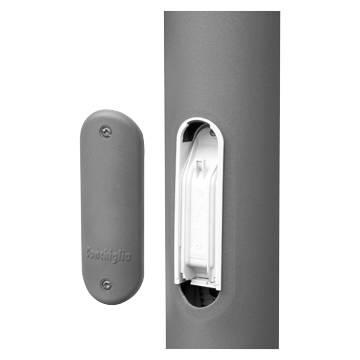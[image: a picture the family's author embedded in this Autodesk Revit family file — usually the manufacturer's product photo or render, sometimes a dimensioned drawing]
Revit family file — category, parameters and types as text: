
# Revit family: Lighting-StreetLighting-GEWISS-STREET[O3]-POLES
name_source: partatom
category: Apparecchi per illuminazione
units: mm (PartAtom-declared; Revit-internal decimal feet)

## family parameters
Condiviso = No
Host = Superficie
Numero OmniClass = 23.80.00.00
Punto di calcolo locali = No
Quota connettore circolare = Usa diametro
Sorgente d'illuminazione = No
Taglio con vuoti quando caricato = No
Tipo di parte = Normale
Titolo OmniClass = Electric Power and Lighting

## types (5) — shared parameters
Altezza palo = 9800 mm  [stored 32.1522 ft]
Catalogue = LIGHTING
Catalogue Range = STREET [O3]
Colour = Graphite grey
Diametro = 60 mm  [stored 0.19685 ft]
Diametro inferiore = 158 mm  [stored 0.518373 ft]
Electrocod = 240
Finishing = Painted
IDF = d4c518be-a0db-4a63-a47f-d3abfb27bd65
IDT = d3b2aa7b-33ea-43be-8ddf-58a48c27c07e
Immagine tipo = GW84096.jpg
Material = Galvanised steel
Palo = <Per categoria>
Produttore = GEWISS S.p.A.
Prospetto di default = 1219 mm
SEO = Pole
Technical sheet = https://www.gewiss.com
Top diameter (mm) = 60
Type: = Conical
URL = https://www.gewiss.com
Version file RFA = 20.11

## per-type parameters (varying)
| type | Base diameter (mm) | Descrizione | EAN code | Modello | Planting (m) | Total length (m) | Weight (kg) | Weight (kg): |
| GW84096 - Galvanised steel - Grey - 5,5m | 115 | STREET CONICAL POLE 5,5m GRAPHITE GREY | 8011564420205 | GW84096 | 0,5 | 5,5 | 45 | 45 |
| GW87593 - Galvanised steel - Grey - 9,8m | 158 | STREET CONICAL POLE 9,8m GRAPHITE GREY | 8011564782594 | GW87593 | 0,8 | 9,8 | 107 | 107 |
| GW87592 - Galvanised steel - Grey - 8,8m | 148 | STREET CONICAL POLE 8,8m GRAPHITE GREY | 8011564782587 | GW87592 | 0,8 | 8,8 | 91 | 91 |
| GW87591 - Galvanised steel - Grey - 6,8m | 128 | STREET CONICAL POLE 6,8m GRAPHITE GREY | 8011564782570 | GW87591 | 0,8 | 6,8 | 48 | 48 |
| GW84097 - Galvanised steel - Grey - 7,8m | 138 | STREET CONICAL POLE 7,8m GRAPHITE GREY | 8011564420212 | GW84097 | 0,8 | 7,8 | 54 | 54 |

note: [stored X ft] marks values corroborated as IEEE doubles in the binary element streams (Revit-internal decimal feet)

## geometry (parser evidence)
native form markers: Blend x2
no freeform markers — native parametric forms only
